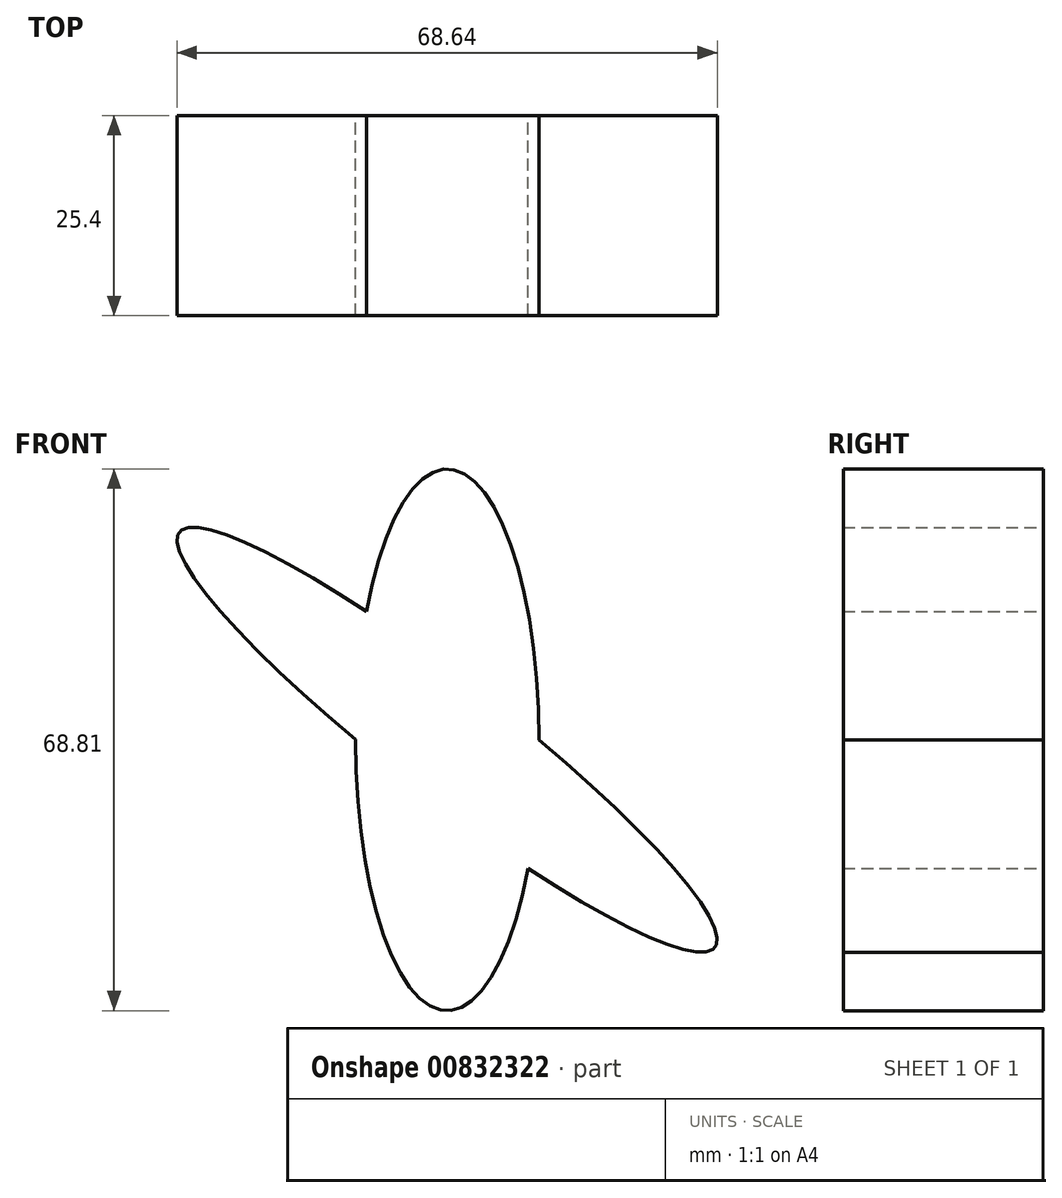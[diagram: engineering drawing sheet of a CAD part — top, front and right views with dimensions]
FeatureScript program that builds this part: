
annotation { "Feature Type Name" : "Feature", "Feature Type Description" : "" }
export const myFeature = defineFeature(function(context is Context, id is Id, definition is map)
    precondition{}
    {
        {
            var Q0;
            Q0=qCreatedBy(makeId("Front.planeOp"),FACE);
            var sketch = newSketch(context, id + "F0", { "sketchPlane" : qUnion([Q0])});
            skEllipse(sketch, "E0", {"center": v(-34.03, 26.37) * mm, "majorRadius": 43.05 * mm, "minorRadius": 7.29 * mm, "majorAxis": v(0.8, -0.61)});
            skEllipse(sketch, "E1", {"center": v(-34.03, 26.37) * mm, "majorRadius": 34.4 * mm, "minorRadius": 11.65 * mm, "majorAxis": v(0, 1)});
            skSolve(sketch);
        }
        {
            var Q0;
            {var subQ0=sQuery(id+"F0.wireOp",EDGE,"E1");var subQ1=sQuery(id+"F0.wireOp",EDGE,"E0");var subQ2=makeQuery(id+"F0.imprint","INTERSECT",VERTEX,{"disambiguationData":[OD(0.0)],"derivedFrom":[subQ1,subQ0]});Q0=makeQuery(id+"F0.imprint","IMPRINT",FACE,{"disambiguationData":[TD([[makeQuery(id+"F0.imprint","IMPRINT",EDGE,{"disambiguationData":[TD([[subQ2,1.0]])],"derivedFrom":subQ1}),-1.0]])]});}
            var Q1;
            {var subQ0=sQuery(id+"F0.wireOp",EDGE,"E1");var subQ1=sQuery(id+"F0.wireOp",EDGE,"E0");var subQ2=makeQuery(id+"F0.imprint","INTERSECT",VERTEX,{"disambiguationData":[OD(2.0)],"derivedFrom":[subQ1,subQ0]});Q1=makeQuery(id+"F0.imprint","IMPRINT",FACE,{"disambiguationData":[TD([[makeQuery(id+"F0.imprint","IMPRINT",EDGE,{"disambiguationData":[TD([[subQ2,-1.0]])],"derivedFrom":subQ1}),-1.0]])]});}
            var Q2;
            {var subQ0=sQuery(id+"F0.wireOp",EDGE,"E1");var subQ1=sQuery(id+"F0.wireOp",EDGE,"E0");var subQ2=makeQuery(id+"F0.imprint","INTERSECT",VERTEX,{"disambiguationData":[OD(0.0)],"derivedFrom":[subQ1,subQ0]});Q2=makeQuery(id+"F0.imprint","IMPRINT",FACE,{"disambiguationData":[TD([[makeQuery(id+"F0.imprint","IMPRINT",EDGE,{"disambiguationData":[TD([[subQ2,-1.0]])],"derivedFrom":subQ1}),1.0]])]});}
            var Q3;
            {var subQ0=sQuery(id+"F0.wireOp",EDGE,"E1");var subQ1=sQuery(id+"F0.wireOp",EDGE,"E0");var subQ2=makeQuery(id+"F0.imprint","INTERSECT",VERTEX,{"disambiguationData":[OD(1.0)],"derivedFrom":[subQ1,subQ0]});Q3=makeQuery(id+"F0.imprint","IMPRINT",FACE,{"disambiguationData":[TD([[makeQuery(id+"F0.imprint","IMPRINT",EDGE,{"disambiguationData":[TD([[subQ2,1.0]])],"derivedFrom":subQ1}),1.0]])]});}
            var Q4;
            {var subQ0=sQuery(id+"F0.wireOp",EDGE,"E1");var subQ1=sQuery(id+"F0.wireOp",EDGE,"E0");var subQ2=makeQuery(id+"F0.imprint","INTERSECT",VERTEX,{"disambiguationData":[OD(0.0)],"derivedFrom":[subQ1,subQ0]});Q4=makeQuery(id+"F0.imprint","IMPRINT",FACE,{"disambiguationData":[TD([[makeQuery(id+"F0.imprint","IMPRINT",EDGE,{"disambiguationData":[TD([[subQ2,1.0]])],"derivedFrom":subQ1}),1.0]])]});}
            extrude(context, id + "F1", {"entities" : qUnion([Q0, Q1, Q2, Q3, Q4]), "depth" : 25.4 * mm, "offsetDistance" : 25.4 * mm});
        }
    });
